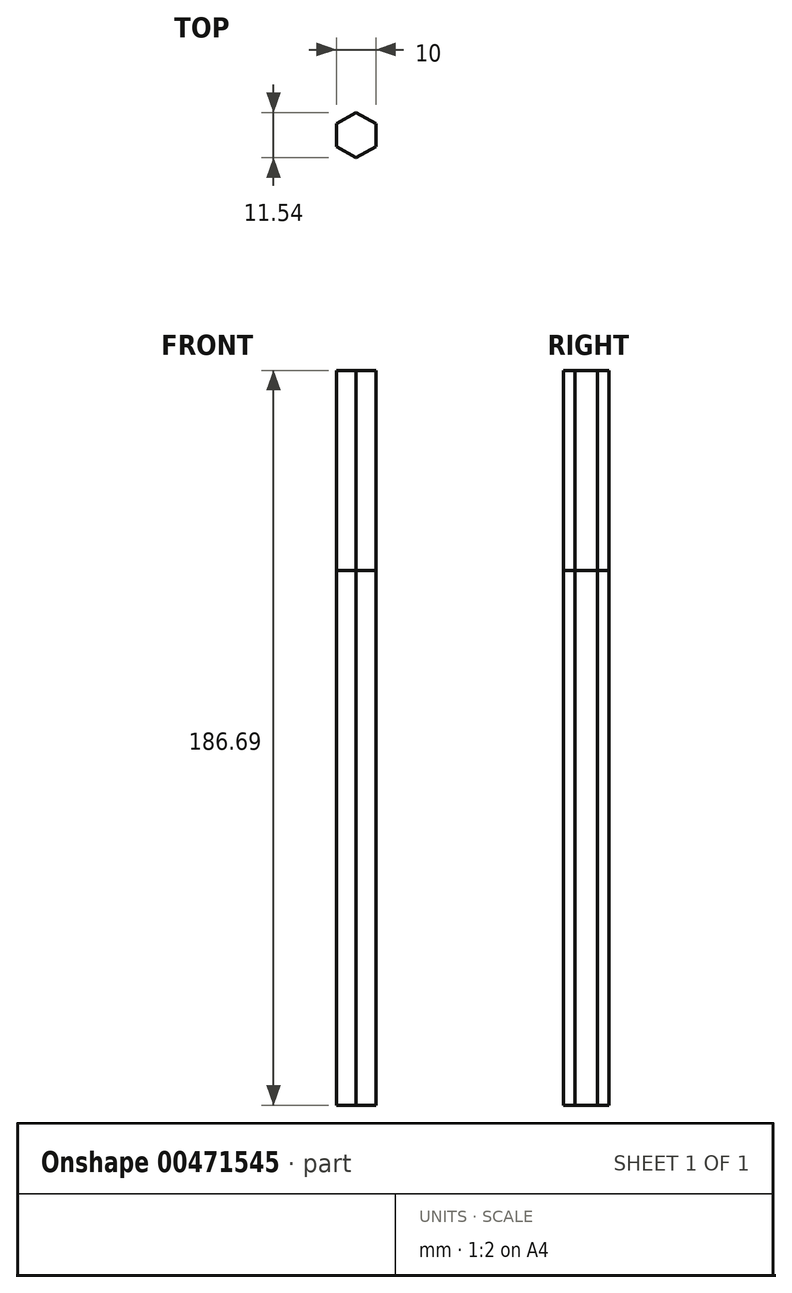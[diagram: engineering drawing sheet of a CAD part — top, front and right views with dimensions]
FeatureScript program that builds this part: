
annotation { "Feature Type Name" : "Feature", "Feature Type Description" : "" }
export const myFeature = defineFeature(function(context is Context, id is Id, definition is map)
    precondition{}
    {
        {
            var Q0;
            Q0=qCreatedBy(makeId("Top.planeOp"),FACE);
            var sketch = newSketch(context, id + "F0", { "sketchPlane" : qUnion([Q0])});
            skCircle(sketch, "E0.cCircle", {"center": v(0, 0) * mm, "radius": 5 * mm, "construction": true});
            skLineSegment(sketch, "E0.0", {"start": v(5, 2.89) * mm, "end": v(5, -2.89) * mm});
            skLineSegment(sketch, "E0.1", {"start": v(5, -2.89) * mm, "end": v(0, -5.77) * mm});
            skLineSegment(sketch, "E0.2", {"start": v(0, -5.77) * mm, "end": v(-5, -2.89) * mm});
            skLineSegment(sketch, "E0.3", {"start": v(-5, -2.89) * mm, "end": v(-5, 2.89) * mm});
            skLineSegment(sketch, "E0.4", {"start": v(-5, 2.89) * mm, "end": v(0, 5.77) * mm});
            skLineSegment(sketch, "E0.5", {"start": v(0, 5.77) * mm, "end": v(5, 2.89) * mm});
            skPoint(sketch, "E0.0.midPoint", {"position": v(5, 0) * mm});
            skSolve(sketch);
        }
        {
            var Q0;
            Q0 = qSketchRegion(id + "F0", true);
            extrude(context, id + "F1", {"entities" : qUnion([Q0]), "oppositeDirection" : true, "depth" : 186.7 * mm});
        }
        {
            var Q0;
            Q0 = qSketchRegion(id + "F0", true);
            extrude(context, id + "F2", {"entities" : qUnion([Q0]), "oppositeDirection" : true, "depth" : 50.8 * mm});
        }
    });
